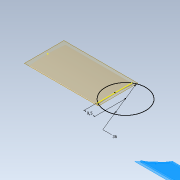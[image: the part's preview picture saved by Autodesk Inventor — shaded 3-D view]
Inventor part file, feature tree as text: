
AUTODESK INVENTOR PART (.ipt)
format: ipt  version: 2021 (Build 250183000, 183)  size: 88,576 bytes
history: native  units: mm
features: other x4, sketch x3, plane x1
ambient origin geometry x8: Origin, YZ Plane, XZ Plane, XY Plane, X Axis, Y Axis, Z Axis, Center Point
bodies: Body1 (feature_tree), Body2 (feature_tree)
feature tree (8):
  other  "Sólido1"
  other  "Superficie reglada1"
  other  "Engrosado1"
  plane  "Plano de trabajo1"
  sketch  "Boceto2"  dims[d1=15.0deg]
  sketch  "Boceto3"  dims[d2=60.0mm d3=0.0mm d4=1.0mm d5=1.0mm d8=36.0mm d9=9.5mm]
  sketch  "Boceto1"  dims[d0=122.0mm]
  other  "Sup1"
